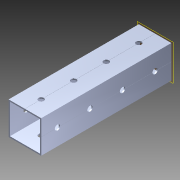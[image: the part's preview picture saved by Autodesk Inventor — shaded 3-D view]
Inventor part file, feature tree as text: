
AUTODESK INVENTOR PART (.ipt)
format: ipt  version: 2014 (Build 180170000, 170)  size: 1,193,984 bytes
history: native  units: in
note: dims shown in document units (in); Inventor stores cm internally (conversion verified against a paired STEP export)
features: extrude x3, sketch x3, pattern_circular x1, other x1, plane x1, imported_body x1
ambient origin geometry x8: Origin, YZ Plane, XZ Plane, XY Plane, X Axis, Y Axis, Z Axis, Center Point
bodies: Body1 (feature_tree)
feature tree (10):
  pattern_circular  "CirPattern2"
  other  "217-3426-STEP1"
  plane  "Work Plane1"
  extrude  "Extrusion1"  Depth=3937.0079in TaperAngle=0.0deg
  extrude  "Extrusion2"  Depth=1.0in TaperAngle=0.0deg
  extrude  "Extrusion3"  [1 undecoded]
  imported_body  "Base1"
  sketch  "Sketch1"  dims[d0=-21.0in d1=3937.0079in d2=0.0in]
  sketch  "Sketch3"  dims[d3=1.0in d4=0.0in d5=16.0in d6=0.0in]
  sketch  "Sketch4"
note: 1 required parameter value undecoded (feature->parameter linkage not recoverable at this tier; creation-order binding heuristic only, values carry confidence <= 0.55)
